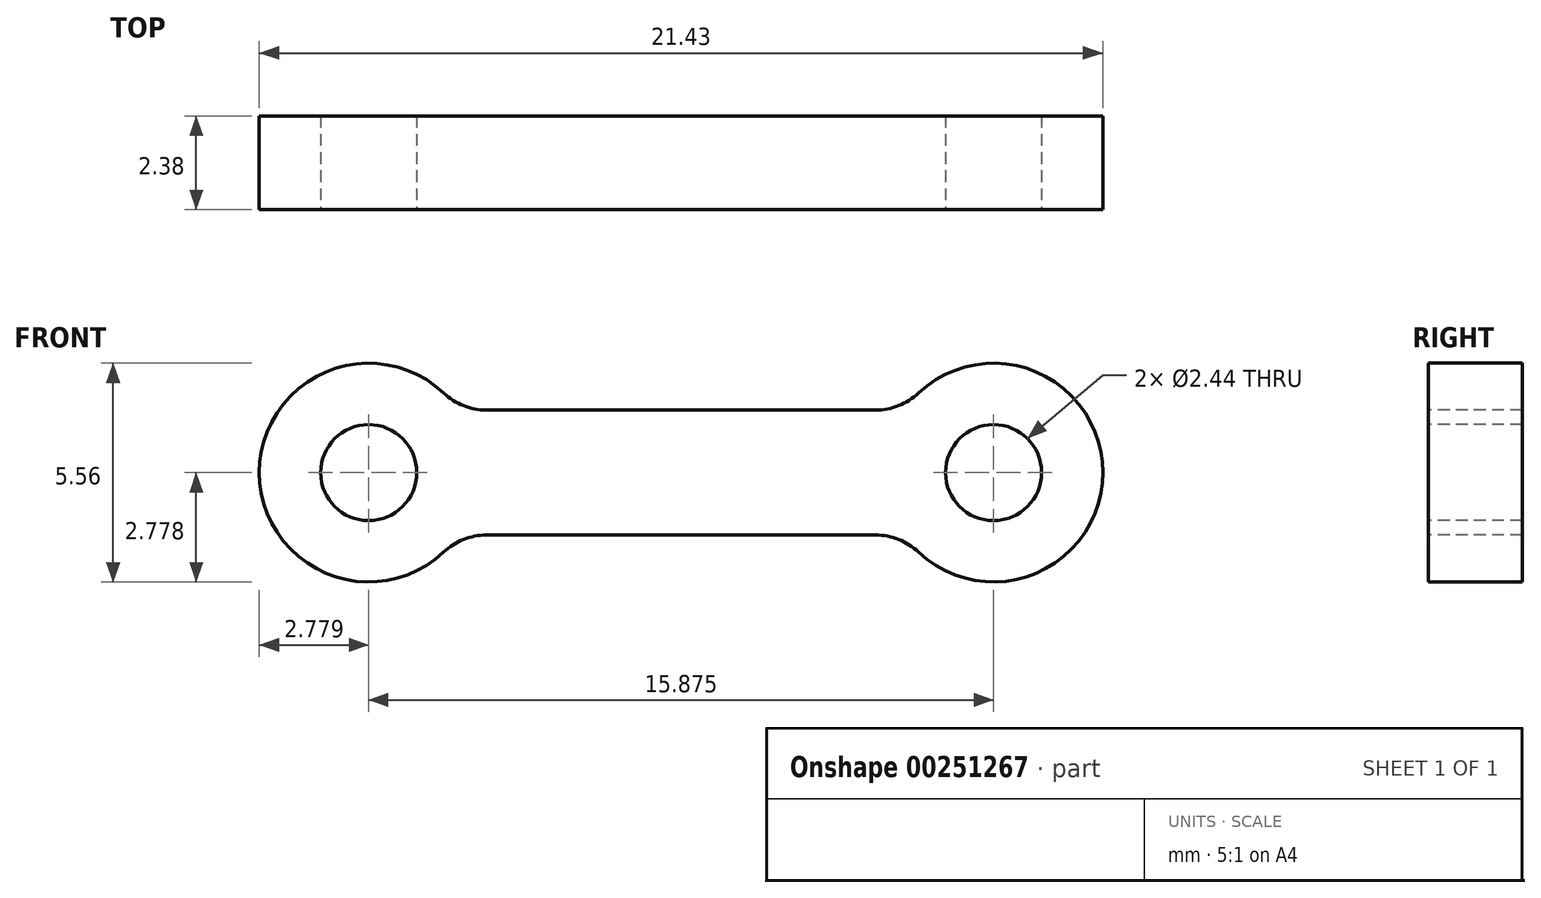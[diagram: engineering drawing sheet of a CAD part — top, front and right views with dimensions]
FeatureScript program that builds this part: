
annotation { "Feature Type Name" : "Feature", "Feature Type Description" : "" }
export const myFeature = defineFeature(function(context is Context, id is Id, definition is map)
    precondition{}
    {
        {
            var Q0;
            Q0=qCreatedBy(makeId("Top.planeOp"),FACE);
            var sketch = newSketch(context, id + "F0", { "sketchPlane" : qUnion([Q0])});
            skLineSegment(sketch, "E0.bottom", {"start": v(5.95, 23.16) * mm, "end": v(27.38, 23.16) * mm});
            skLineSegment(sketch, "E0.top", {"start": v(5.95, 20.78) * mm, "end": v(27.38, 20.78) * mm});
            skLineSegment(sketch, "E0.left", {"start": v(5.95, 23.16) * mm, "end": v(5.95, 20.78) * mm});
            skLineSegment(sketch, "E0.right", {"start": v(27.38, 23.16) * mm, "end": v(27.38, 20.78) * mm});
            skSolve(sketch);
        }
        {
            var Q0;
            Q0 = qSketchRegion(id + "F0", true);
            extrude(context, id + "F1", {"entities" : qUnion([Q0]), "depth" : 5.56 * mm});
        }
        {
            var Q0;
            Q0=makeQuery(id+"F1.opExtrude","CAP_EDGE",EDGE,{"disambiguationData":[OSD([sQuery(id+"F0.wireOp",EDGE,"E0.right")])],"isStart":false});
            var Q1;
            Q1=makeQuery(id+"F1.opExtrude","CAP_EDGE",EDGE,{"disambiguationData":[OSD([sQuery(id+"F0.wireOp",EDGE,"E0.right")])],"isStart":true});
            var Q2;
            Q2=makeQuery(id+"F1.opExtrude","CAP_EDGE",EDGE,{"disambiguationData":[OSD([sQuery(id+"F0.wireOp",EDGE,"E0.left")])],"isStart":false});
            var Q3;
            Q3=makeQuery(id+"F1.opExtrude","CAP_EDGE",EDGE,{"disambiguationData":[OSD([sQuery(id+"F0.wireOp",EDGE,"E0.left")])],"isStart":true});
            fillet(context, id + "F2", {"entities" : qUnion([Q0, Q1, Q2, Q3]), "radius" : 2.78 * mm, "tangentPropagation" : true, "allowEdgeOverflow" : false});
        }
        {
            var Q0;
            Q0=makeQuery(id+"F1.opExtrude","SWEPT_FACE",FACE,{"disambiguationData":[OSD([sQuery(id+"F0.wireOp",EDGE,"E0.top")])]});
            var sketch = newSketch(context, id + "F3", { "sketchPlane" : qUnion([Q0])});
            skCircle(sketch, "E1", {"center": v(8.73, 2.78) * mm, "radius": 1.22 * mm});
            skCircle(sketch, "E2", {"center": v(24.6, 2.78) * mm, "radius": 1.22 * mm});
            skArc(sketch, "E3", {"start": v(8.73, 0) * mm, "mid": v(11.5, 2.78) * mm, "end": v(8.73, 5.56) * mm});
            skArc(sketch, "E4", {"start": v(24.6, 5.56) * mm, "mid": v(21.83, 2.78) * mm, "end": v(24.6, 0) * mm});
            skLineSegment(sketch, "E5", {"start": v(11, 4.37) * mm, "end": v(22.32, 4.37) * mm});
            skLineSegment(sketch, "E6", {"start": v(11, 1.2) * mm, "end": v(22.32, 1.2) * mm});
            skArc(sketch, "E7", {"start": v(10.64, 4.8) * mm, "mid": v(11.14, 4.48) * mm, "end": v(11.73, 4.37) * mm});
            skArc(sketch, "E8", {"start": v(11.73, 1.2) * mm, "mid": v(11.14, 1.08) * mm, "end": v(10.64, 0.76) * mm});
            skArc(sketch, "E9", {"start": v(21.6, 4.37) * mm, "mid": v(22.2, 4.48) * mm, "end": v(22.7, 4.8) * mm});
            skArc(sketch, "E10", {"start": v(22.7, 0.76) * mm, "mid": v(22.2, 1.08) * mm, "end": v(21.6, 1.2) * mm});
            skSolve(sketch);
        }
        {
            var Q0;
            Q0=makeQuery(id+"F3.imprint","IMPRINT",FACE,{"disambiguationData":[TD([[makeQuery(id+"F3.imprint","IMPRINT",EDGE,{"derivedFrom":sQuery(id+"F3.wireOp",EDGE,"E1")}),1.0]])]});
            var Q1;
            Q1=makeQuery(id+"F3.imprint","IMPRINT",FACE,{"disambiguationData":[TD([[makeQuery(id+"F3.imprint","IMPRINT",EDGE,{"derivedFrom":sQuery(id+"F3.wireOp",EDGE,"E2")}),1.0]])]});
            var Q2;
            {var subQ0=sQuery(id+"F3.wireOp",EDGE,"E7");Q2=makeQuery(id+"F3.imprint","IMPRINT",FACE,{"disambiguationData":[TD([[makeQuery(id+"F3.imprint","IMPRINT",EDGE,{"derivedFrom":subQ0}),1.0]])]});}
            var Q3;
            {var subQ0=sQuery(id+"F3.wireOp",EDGE,"E8");Q3=makeQuery(id+"F3.imprint","IMPRINT",FACE,{"disambiguationData":[TD([[makeQuery(id+"F3.imprint","IMPRINT",EDGE,{"derivedFrom":subQ0}),1.0]])]});}
            extrude(context, id + "F4", {"entities" : qUnion([Q0, Q1, Q2, Q3]), "operationType" : NewBodyOperationType.REMOVE, "oppositeDirection" : true, "depth" : 25.4 * mm});
        }
    });
